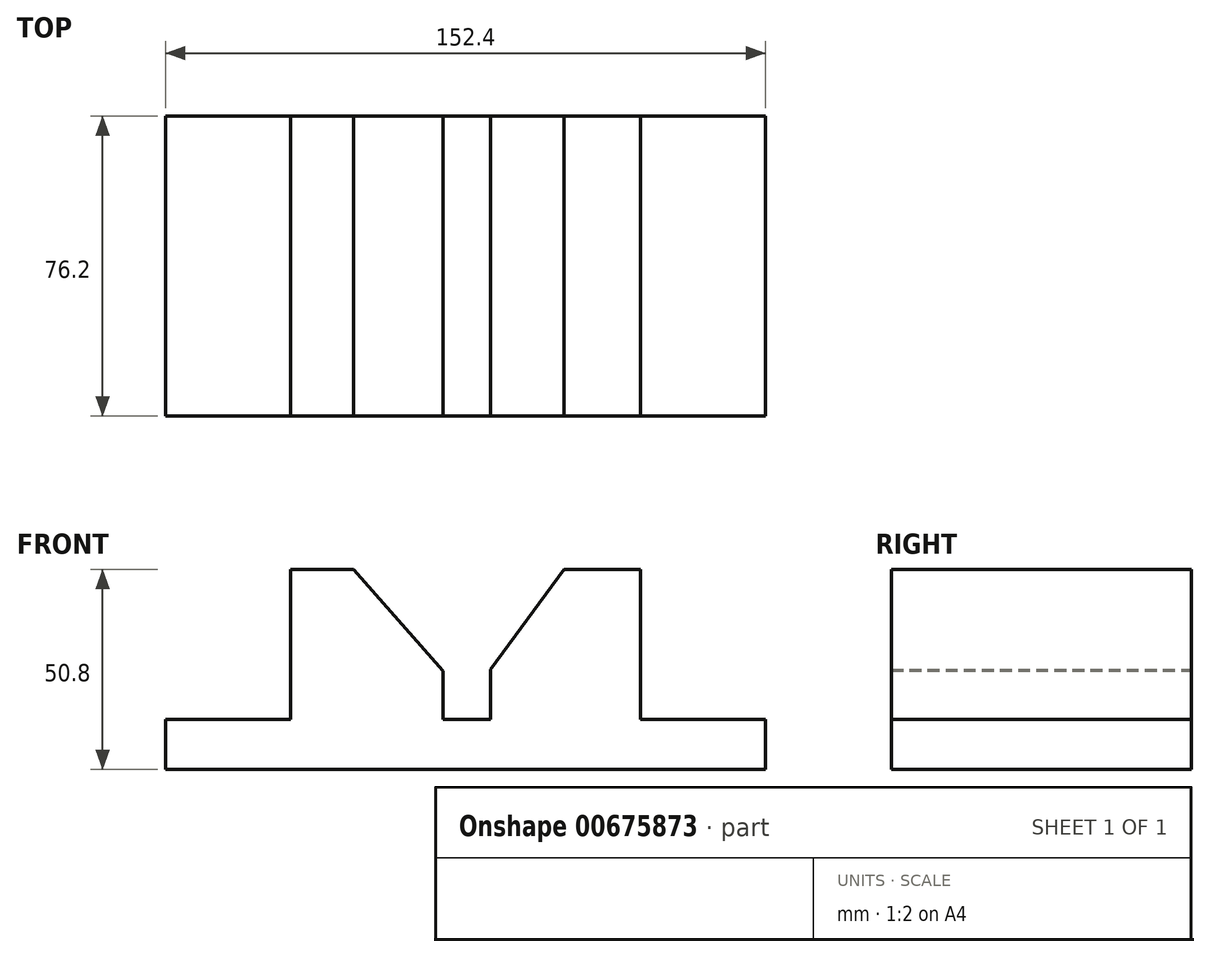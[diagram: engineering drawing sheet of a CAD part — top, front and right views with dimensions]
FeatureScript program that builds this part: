
annotation { "Feature Type Name" : "Feature", "Feature Type Description" : "" }
export const myFeature = defineFeature(function(context is Context, id is Id, definition is map)
    precondition{}
    {
        {
            var Q0;
            Q0=qCreatedBy(makeId("Front.planeOp"),FACE);
            var sketch = newSketch(context, id + "F0", { "sketchPlane" : qUnion([Q0])});
            skLineSegment(sketch, "E0", {"start": v(-77.12, -3.73) * mm, "end": v(-77.12, -41.83) * mm});
            skLineSegment(sketch, "E1", {"start": v(-77.12, -41.83) * mm, "end": v(-108.87, -41.83) * mm});
            skLineSegment(sketch, "E2", {"start": v(-108.87, -41.83) * mm, "end": v(-108.87, -54.53) * mm});
            skLineSegment(sketch, "E3", {"start": v(-108.87, -54.53) * mm, "end": v(43.53, -54.53) * mm});
            skLineSegment(sketch, "E4", {"start": v(43.53, -54.53) * mm, "end": v(43.53, -41.83) * mm});
            skLineSegment(sketch, "E5", {"start": v(43.53, -41.83) * mm, "end": v(11.78, -41.83) * mm});
            skLineSegment(sketch, "E6", {"start": v(11.78, -41.83) * mm, "end": v(11.78, -3.73) * mm});
            skLineSegment(sketch, "E7", {"start": v(-39.02, -41.83) * mm, "end": v(-26.32, -41.83) * mm});
            skLineSegment(sketch, "E8", {"start": v(-38.42, -42.16) * mm, "end": v(-38.42, -29.46) * mm});
            skLineSegment(sketch, "E9", {"start": v(-26.32, -41.83) * mm, "end": v(-26.32, -29.13) * mm});
            skLineSegment(sketch, "E10", {"start": v(11.78, -3.73) * mm, "end": v(-7.63, -3.73) * mm});
            skLineSegment(sketch, "E11", {"start": v(-77.12, -3.73) * mm, "end": v(-61.16, -3.73) * mm});
            skLineSegment(sketch, "E12", {"start": v(-61.16, -3.73) * mm, "end": v(-38.42, -29.46) * mm});
            skLineSegment(sketch, "E13", {"start": v(-26.32, -29.13) * mm, "end": v(-7.63, -3.73) * mm});
            skSolve(sketch);
        }
        {
            var Q0;
            Q0=makeQuery(id+"F0.imprint","IMPRINT",FACE,{"disambiguationData":[TD([[makeQuery(id+"F0.imprint","IMPRINT",EDGE,{"derivedFrom":sQuery(id+"F0.wireOp",EDGE,"E0")}),1.0]])]});
            extrude(context, id + "F1", {"entities" : qUnion([Q0]), "depth" : 76.2 * mm, "offsetDistance" : 25.4 * mm});
        }
    });
